# Revit family: Legrand_Drivia_residential_box_13_modules
name_source: partatom
category: Equipement électrique
revit_build: Autodesk Revit 2018 (Build: 20170223_1515(x64)
units: mm (PartAtom-declared; Revit-internal decimal feet)

## family parameters
Basée sur le plan de construction = Non
Configuration du panneau = Deux colonnes, circuits au sein
Cote de connecteur circulaire = Utiliser le diamètre
Couper avec des vides une fois chargée = Non
Numéro OmniClass = 23.80.30.11.17
Partagée = Non
Point de calcul de pièce = Non
Titre OmniClass = Distribution Boards and Control Panels
Toujours verticalement = Oui
Type d'élément = Tableau de raccordement

## types (4) — shared parameters
ETIM Class 6.0 = EC000214
Fabricant = Legrand
General Conditions of Use = https://export.legrand.com
ICC = 10000 A
IK = 05
IP = 30
Material = shock polystyrene
RAL = 9003
Tension = 400V AC - 50/60 Hz
UIMP = 6000 V
URL = www.legrand.fr
depth = 104 mm
depth installation zone = 207 mm  [stored 0.679134 ft]
distance before installation zone = 104 mm
distance side installation zone = 250 mm  [stored 0.82021 ft]
self-extinguishing = 750 °C
transparent door = Non
transparent door 401341 = Non
transparent door 401342 = Non
transparent door 401343 = Non
transparent door 401344 = Non
white door = Non
white door 401331 = Non
white door 401332 = Non
white door 401333 = Non
white door 401334 = Non
width = 250 mm  [stored 0.82021 ft]
width installation zone = 750 mm  [stored 2.46063 ft]

## per-type parameters (varying)
| type | Cabinet 401211 | Cabinet 401212 | Cabinet 401213 | Cabinet 401214 | Description | Image du type | height | power max allowable |
| Legrand Drivia residential plastic box 1 row 13 modules | Oui | Non | Non | Non | 401211 Legrand Drivia residential plastic box 1 row 13 modules | Drivia_1rangee_13m_401211_pw_206357_pz_1.jpg | 250 mm  [stored 0.82021 ft] | 60 A |
| Legrand Drivia residential plastic box 2 rows 13 modules | Non | Oui | Non | Non | 401212 Legrand Drivia residential plastic box 2 rows 13 modules | Drivia_2rangee_13m_401211_pw_206357_pz_1.jpg | 375 mm  [stored 1.23031 ft] | 90 A |
| Legrand Drivia residential plastic box 3 rows 13 modules | Non | Non | Oui | Non | 401213 Legrand Drivia residential plastic box 3 rows 13 modules | Drivia_3rangees_401213_pw_206551_pz_1.jpg | 500 mm  [stored 1.64042 ft] | 90 A |
| Legrand Drivia residential plastic box 4 rows 13 modules | Non | Non | Non | Oui | 401214 Legrand Drivia residential plastic box 4 rows 13 modules | Drivia_4rangees_13m_401211_pw_206357_pz_1.jpg | 625 mm  [stored 2.05052 ft] | 90 A |

note: [stored X ft] marks values corroborated as IEEE doubles in the binary element streams (Revit-internal decimal feet)
